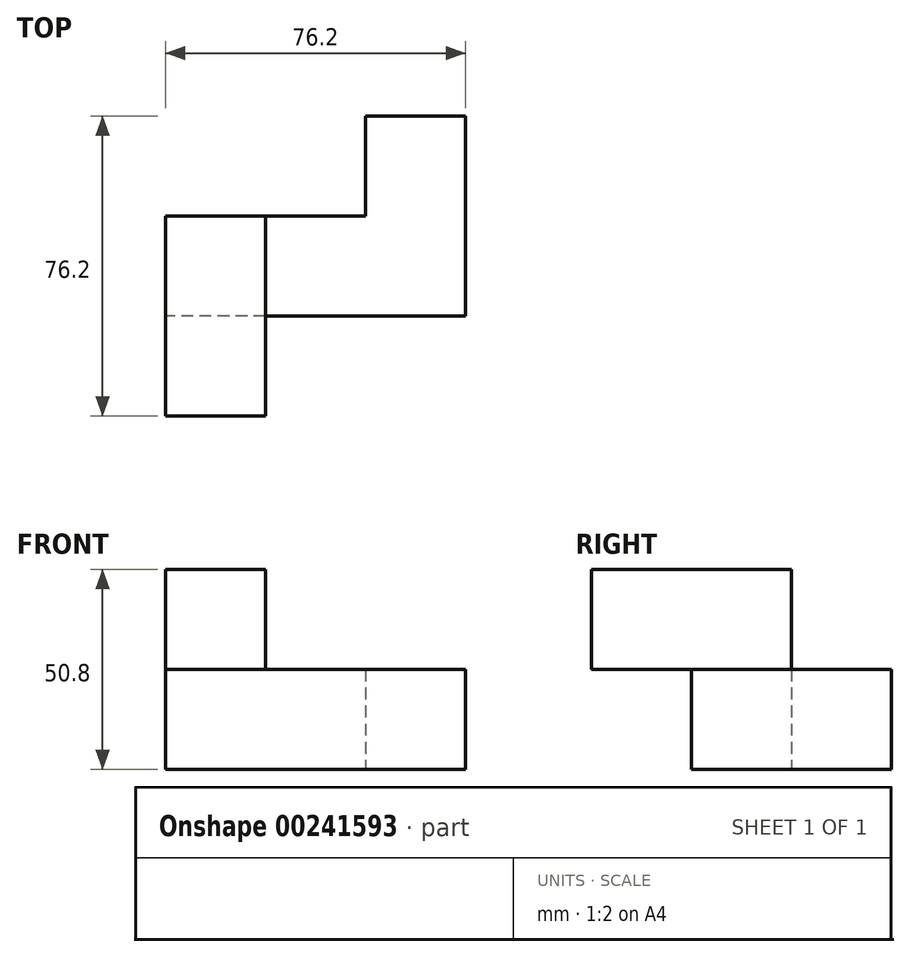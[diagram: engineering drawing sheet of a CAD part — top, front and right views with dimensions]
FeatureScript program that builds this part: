
annotation { "Feature Type Name" : "Feature", "Feature Type Description" : "" }
export const myFeature = defineFeature(function(context is Context, id is Id, definition is map)
    precondition{}
    {
        {
            var Q0;
            Q0=qCreatedBy(makeId("Front.planeOp"),FACE);
            var sketch = newSketch(context, id + "F0", { "sketchPlane" : qUnion([Q0])});
            skLineSegment(sketch, "E0.bottom", {"start": v(-32.8, 8.21) * mm, "end": v(43.4, 8.21) * mm});
            skLineSegment(sketch, "E0.top", {"start": v(-32.8, -17.19) * mm, "end": v(43.4, -17.19) * mm});
            skLineSegment(sketch, "E0.left", {"start": v(-32.8, 8.21) * mm, "end": v(-32.8, -17.19) * mm});
            skLineSegment(sketch, "E0.right", {"start": v(43.4, 8.21) * mm, "end": v(43.4, -17.19) * mm});
            skSolve(sketch);
        }
        {
            var Q0;
            Q0=makeQuery(id+"F0.imprint","IMPRINT",FACE,{"disambiguationData":[TD([[makeQuery(id+"F0.imprint","IMPRINT",EDGE,{"derivedFrom":sQuery(id+"F0.wireOp",EDGE,"E0.bottom")}),-1.0]])]});
            extrude(context, id + "F1", {"entities" : qUnion([Q0]), "depth" : 25.4 * mm});
        }
        {
            var Q0;
            Q0=makeQuery(id+"F1.opExtrude","CAP_FACE",FACE,{"disambiguationData":[OSD([sQuery(id+"F0.wireOp",EDGE,"E0.bottom"),sQuery(id+"F0.wireOp",EDGE,"E0.top"),sQuery(id+"F0.wireOp",EDGE,"E0.left"),sQuery(id+"F0.wireOp",EDGE,"E0.right")])],"isStart":true});
            var sketch = newSketch(context, id + "F2", { "sketchPlane" : qUnion([Q0])});
            skLineSegment(sketch, "E1.bottom", {"start": v(-43.4, 8.21) * mm, "end": v(-18, 8.21) * mm});
            skLineSegment(sketch, "E1.top", {"start": v(-43.4, -17.19) * mm, "end": v(-18, -17.19) * mm});
            skLineSegment(sketch, "E1.left", {"start": v(-43.4, 8.21) * mm, "end": v(-43.4, -17.19) * mm});
            skLineSegment(sketch, "E1.right", {"start": v(-18, 8.21) * mm, "end": v(-18, -17.19) * mm});
            skSolve(sketch);
        }
        {
            var Q0;
            Q0=makeQuery(id+"F2.imprint","IMPRINT",FACE,{"disambiguationData":[TD([[makeQuery(id+"F2.imprint","IMPRINT",EDGE,{"derivedFrom":sQuery(id+"F2.wireOp",EDGE,"E1.bottom")}),1.0]])]});
            extrude(context, id + "F3", {"entities" : qUnion([Q0]), "operationType" : NewBodyOperationType.ADD, "depth" : 25.4 * mm});
        }
        {
            var Q0;
            Q0=makeQuery(id+"F3.boolean.opBoolean","MERGE",FACE,{"derivedFrom":[makeQuery(id+"F1.opExtrude","SWEPT_FACE",FACE,{"disambiguationData":[OSD([sQuery(id+"F0.wireOp",EDGE,"E0.bottom")])]}),makeQuery(id+"F3.opExtrude","SWEPT_FACE",FACE,{"disambiguationData":[OSD([sQuery(id+"F2.wireOp",EDGE,"E1.bottom")])]})]});
            var sketch = newSketch(context, id + "F4", { "sketchPlane" : qUnion([Q0])});
            skLineSegment(sketch, "E2.bottom", {"start": v(-7.4, -25.4) * mm, "end": v(-32.8, -25.4) * mm});
            skLineSegment(sketch, "E2.top", {"start": v(-7.4, 0) * mm, "end": v(-32.8, 0) * mm});
            skLineSegment(sketch, "E2.left", {"start": v(-7.4, -25.4) * mm, "end": v(-7.4, 0) * mm});
            skLineSegment(sketch, "E2.right", {"start": v(-32.8, -25.4) * mm, "end": v(-32.8, 0) * mm});
            skSolve(sketch);
        }
        {
            var Q0;
            Q0=makeQuery(id+"F4.imprint","IMPRINT",FACE,{"disambiguationData":[TD([[makeQuery(id+"F4.imprint","IMPRINT",EDGE,{"derivedFrom":sQuery(id+"F4.wireOp",EDGE,"E2.bottom")}),1.0]])]});
            extrude(context, id + "F5", {"entities" : qUnion([Q0]), "operationType" : NewBodyOperationType.ADD, "depth" : 25.4 * mm});
        }
        {
            var Q0;
            Q0=makeQuery(id+"F5.boolean.opBoolean","MERGE",FACE,{"derivedFrom":[makeQuery(id+"F1.opExtrude","CAP_FACE",FACE,{"disambiguationData":[OSD([sQuery(id+"F0.wireOp",EDGE,"E0.bottom"),sQuery(id+"F0.wireOp",EDGE,"E0.top"),sQuery(id+"F0.wireOp",EDGE,"E0.left"),sQuery(id+"F0.wireOp",EDGE,"E0.right")])],"isStart":false}),makeQuery(id+"F5.opExtrude","SWEPT_FACE",FACE,{"disambiguationData":[OSD([sQuery(id+"F4.wireOp",EDGE,"E2.bottom")])]})]});
            var sketch = newSketch(context, id + "F6", { "sketchPlane" : qUnion([Q0])});
            skLineSegment(sketch, "E3.bottom", {"start": v(-7.4, 8.21) * mm, "end": v(-32.8, 8.21) * mm});
            skLineSegment(sketch, "E3.top", {"start": v(-7.4, 33.61) * mm, "end": v(-32.8, 33.61) * mm});
            skLineSegment(sketch, "E3.left", {"start": v(-7.4, 8.21) * mm, "end": v(-7.4, 33.61) * mm});
            skLineSegment(sketch, "E3.right", {"start": v(-32.8, 8.21) * mm, "end": v(-32.8, 33.61) * mm});
            skSolve(sketch);
        }
        {
            var Q0;
            Q0=makeQuery(id+"F6.imprint","IMPRINT",FACE,{"disambiguationData":[TD([[makeQuery(id+"F6.imprint","IMPRINT",EDGE,{"derivedFrom":sQuery(id+"F6.wireOp",EDGE,"E3.bottom")}),-1.0]])]});
            extrude(context, id + "F7", {"entities" : qUnion([Q0]), "operationType" : NewBodyOperationType.ADD, "depth" : 25.4 * mm});
        }
    });
